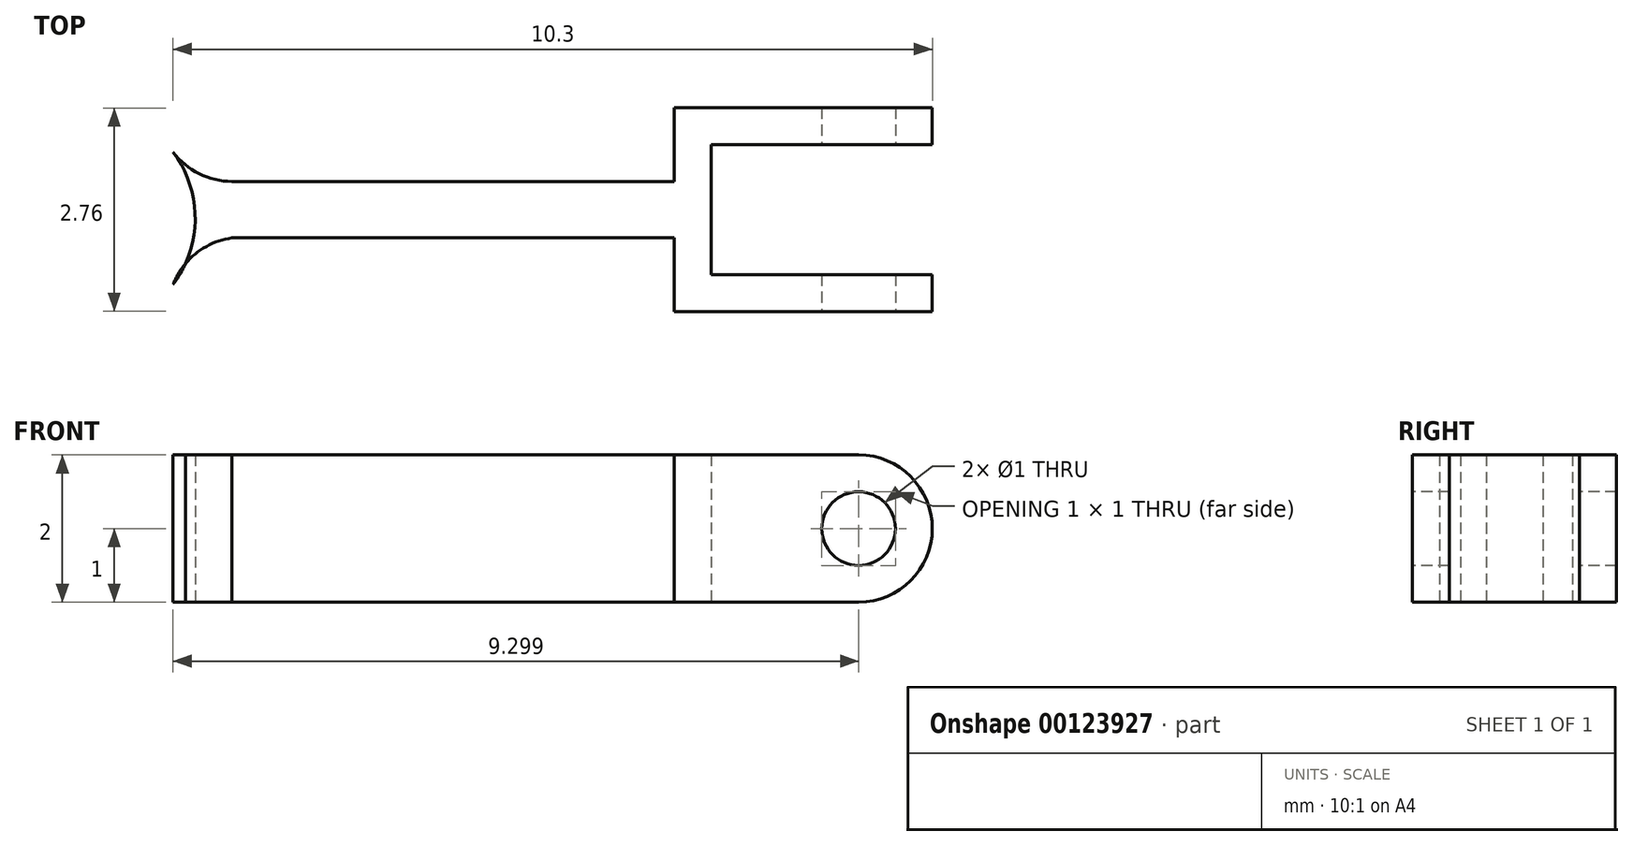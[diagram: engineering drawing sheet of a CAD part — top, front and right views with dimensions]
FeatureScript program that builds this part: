
annotation { "Feature Type Name" : "Feature", "Feature Type Description" : "" }
export const myFeature = defineFeature(function(context is Context, id is Id, definition is map)
    precondition{}
    {
        {
            var Q0;
            Q0=qCreatedBy(makeId("Top.planeOp"),FACE);
            var sketch = newSketch(context, id + "F0", { "sketchPlane" : qUnion([Q0])});
            skArc(sketch, "E0", {"start": v(2.4, 18.75) * mm, "mid": v(2.75, 18.46) * mm, "end": v(3.2, 18.35) * mm});
            skArc(sketch, "E1", {"start": v(3.2, 17.59) * mm, "mid": v(2.71, 17.38) * mm, "end": v(2.4, 16.95) * mm});
            skArc(sketch, "E2", {"start": v(2.4, 16.95) * mm, "mid": v(2.7, 17.85) * mm, "end": v(2.4, 18.75) * mm});
            skLineSegment(sketch, "E3", {"start": v(3.2, 18.35) * mm, "end": v(9.2, 18.35) * mm});
            skLineSegment(sketch, "E4", {"start": v(3.2, 17.59) * mm, "end": v(9.2, 17.59) * mm});
            skLineSegment(sketch, "E5", {"start": v(9.2, 18.35) * mm, "end": v(9.2, 19.35) * mm});
            skLineSegment(sketch, "E6", {"start": v(9.2, 19.35) * mm, "end": v(11.7, 19.35) * mm});
            skLineSegment(sketch, "E7", {"start": v(11.7, 19.35) * mm, "end": v(11.7, 18.85) * mm});
            skLineSegment(sketch, "E8", {"start": v(11.7, 18.85) * mm, "end": v(9.7, 18.85) * mm});
            skLineSegment(sketch, "E9", {"start": v(9.7, 18.85) * mm, "end": v(9.7, 17.09) * mm});
            skLineSegment(sketch, "E10", {"start": v(9.7, 17.09) * mm, "end": v(11.7, 17.09) * mm});
            skLineSegment(sketch, "E11", {"start": v(11.7, 17.09) * mm, "end": v(11.7, 16.59) * mm});
            skLineSegment(sketch, "E12", {"start": v(11.7, 16.59) * mm, "end": v(9.2, 16.59) * mm});
            skLineSegment(sketch, "E13", {"start": v(9.2, 16.59) * mm, "end": v(9.2, 17.59) * mm});
            skSolve(sketch);
        }
        {
            var Q0;
            Q0 = qSketchRegion(id + "F0", true);
            extrude(context, id + "F1", {"entities" : qUnion([Q0]), "depth" : 2 * mm});
        }
        {
            var Q0;
            Q0=makeQuery(id+"F1.opExtrude","SWEPT_FACE",FACE,{"disambiguationData":[OSD([sQuery(id+"F0.wireOp",EDGE,"E12")])]});
            var sketch = newSketch(context, id + "F2", { "sketchPlane" : qUnion([Q0])});
            skPoint(sketch, "E14.centerSnap0", {"position": v(9.2, 1) * mm});
            skCircle(sketch, "E15", {"center": v(11.7, 1) * mm, "radius": 1 * mm});
            skLineSegment(sketch, "E16.0.0", {"start": v(9.7, 0) * mm, "end": v(11.7, 0) * mm});
            skLineSegment(sketch, "E16.0.1", {"start": v(11.7, 0) * mm, "end": v(11.7, 2) * mm});
            skLineSegment(sketch, "E16.0.2", {"start": v(11.7, 2) * mm, "end": v(9.7, 2) * mm});
            skLineSegment(sketch, "E16.0.3", {"start": v(9.7, 2) * mm, "end": v(9.7, 0) * mm});
            skSolve(sketch);
        }
        {
            var Q0;
            Q0 = qSketchRegion(id + "F2", true);
            extrude(context, id + "F3", {"entities" : qUnion([Q0]), "operationType" : NewBodyOperationType.ADD, "oppositeDirection" : true, "depth" : 0.5 * mm});
        }
        {
            var Q0;
            Q0=makeQuery(id+"F1.opExtrude","SWEPT_FACE",FACE,{"disambiguationData":[OSD([sQuery(id+"F0.wireOp",EDGE,"E8")])]});
            var sketch = newSketch(context, id + "F4", { "sketchPlane" : qUnion([Q0])});
            skCircle(sketch, "E17", {"center": v(11.7, 1) * mm, "radius": 1 * mm});
            skSolve(sketch);
        }
        {
            var Q0;
            {var subQ1=sQuery(id+"F0.wireOp",EDGE,"E8");var subQ2=makeQuery(id+"F1.opExtrude","SWEPT_EDGE",EDGE,{"disambiguationData":[OSD([sQuery(id+"F0.wireOp",EDGE,"E7"),subQ1])]});Q0=makeQuery(id+"F4.imprint","IMPRINT",FACE,{"disambiguationData":[TD([[makeQuery(id+"F4.imprint","IMPRINT",EDGE,{"derivedFrom":subQ2}),1.0]])]});}
            extrude(context, id + "F5", {"entities" : qUnion([Q0]), "operationType" : NewBodyOperationType.ADD, "oppositeDirection" : true, "depth" : 0.5 * mm});
        }
        {
            var Q0;
            Q0=makeQuery(id+"F3.boolean.opBoolean","MERGE",FACE,{"derivedFrom":[makeQuery(id+"F1.opExtrude","SWEPT_FACE",FACE,{"disambiguationData":[OSD([sQuery(id+"F0.wireOp",EDGE,"E12")])]}),makeQuery(id+"F3.opExtrude","CAP_FACE",FACE,{"disambiguationData":[OSD([sQuery(id+"F2.wireOp",EDGE,"E15"),sQuery(id+"F2.wireOp",EDGE,"E16.0.0"),sQuery(id+"F2.wireOp",EDGE,"E16.0.2"),sQuery(id+"F2.wireOp",EDGE,"E16.0.3")])],"isStart":true})]});
            var sketch = newSketch(context, id + "F6", { "sketchPlane" : qUnion([Q0])});
            skCircle(sketch, "E18", {"center": v(11.7, 1) * mm, "radius": 0.5 * mm});
            skSolve(sketch);
        }
        {
            var Q0;
            Q0 = qSketchRegion(id + "F6", true);
            extrude(context, id + "F7", {"entities" : qUnion([Q0]), "operationType" : NewBodyOperationType.REMOVE, "oppositeDirection" : true, "depth" : 25 * mm});
        }
    });
